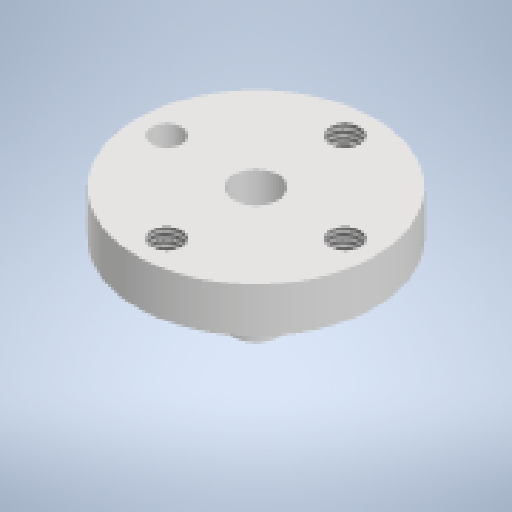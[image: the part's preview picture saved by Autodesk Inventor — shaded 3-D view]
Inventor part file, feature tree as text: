
AUTODESK INVENTOR PART (.ipt)
format: ipt  version: 2024.2 (Build 282272000, 272)  size: 250,880 bytes
history: native  units: mm
features: thread x3, extrude x2, other x1, sketch x1
ambient origin geometry x8: Origin, YZ Plane, XZ Plane, XY Plane, X Axis, Y Axis, Z Axis, Center Point
bodies: Body1 (feature_tree)
feature tree (7):
  other  "Твердое тело1"
  sketch  "Эскиз1"
  extrude  "Выдавливание1"  Depth=16.0mm
  extrude  "Выдавливание2"  Depth=2.0mm
  thread  "Резьба1"
  thread  "Резьба2"
  thread  "Резьба3"
